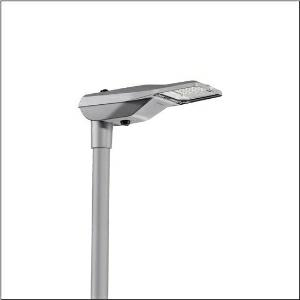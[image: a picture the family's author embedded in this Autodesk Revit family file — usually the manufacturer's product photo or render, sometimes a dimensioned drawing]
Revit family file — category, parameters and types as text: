
# Revit family: streetlight_sl_21_micro___p0_8a_5xe1u33t08db_8449
name_source: partatom
category: Lighting Fixtures
units: mm (PartAtom-declared; Revit-internal decimal feet)

## family parameters
Cut with Voids When Loaded = No
Host = Face
Light Source = No
Part Type = Normal
Room Calculation Point = No
Round Connector Dimension = Use Diameter
Shared = No

## types (1)
- --- (1 x LED, 5040 lm, 39.1 W, 3000K)
    Apparent Load = 39 VA
    CIE Flux Codes = 33 69 96 100 100
    Color Rendering = 70
    Color Temperature = 3000K
    Default Elevation = 1800 mm
    Description = Streetlight SL 21 micro, mast luminaire, primary light control with lens, of PMMA, primary optical cover: cover, of toughened safety glass, transparent, light distribution: P0.8a, light emission: direct distribution, primary light characteristic: asymmetric, installation type: post-top, side-entry, LED, High Power LED, rated luminous flux: 5.040lm, luminous efficacy: 129lm/W, light colour: 730, colour temperature: 3000K, control gear: D4i, control: pre-setting: logarithmic dimming characteristic, flexible luminous flux parameterisation, time-dependent luminous flux control, constant luminous flux control, overheat protection, mains connection: 220..240V, AC, 50/60Hz, start of lifetime: 39W, end of service life: 41W, reduction: 18W, luminaire housing, of diecast aluminium, powder-coated, Siteco® metallic grey (DB 702S), corrosivity category C5 mid according to DIN EN ISO 12944, multi-level sealing system, sealing non-destructively replaceable, inclination adjustable: 0°, 5°, 10°, 15°, please order mast flange separately, length: 528mm, width: 235mm, height: 110mm, mast flange for spigot size: 42mm (side-entry): 5XC10008XM4, 60/48mm (side-entry/post-top): 5XC10108XM2, 76/60mm (side-entry/post-top): 5XC10108XM1, Smart Interface below and above, protection rating (complete): IP66, insulation class (complete): insulation class II (safety insulation), certification: CE, ENEC, ENEC+, VDE, impact resistance: IK10, permissible operating ambient temperature for outdoor applications: -40..+50°C, standard-compliant lighting for roads and squares, packaging unit: 1 piece

Light Distribution: P0.8a
    Height = 110 mm
    Lamp = 1 x LED
    Lamp Light Flux = 5040 lm
    Lamp Power = 39.1 W
    Lamp count = 1
    Length = 528 mm
    Luminous efficacy = 129 lm/W
    Manufacturer = Siteco
    ModVariant = No
    Model = 5XE1U33T08DB
    Number of Poles = 1
    OnlyDefault = Yes
    Power Factor = 1
    Product Name = Streetlight SL 21 micro | P0.8a
    Product group = mast luminaire | pylon top
    ProductGroupID = 6100
    Protection Class = Protection class II
    Protection Degree = IP 66
    RLX_Detail_Level = 1
    RLX_Emergency_Light_Flux = 0 lm
    RLX_Emergency_Type = 0
    RLX_Emergency_Type_DB = No
    RlxData = <blob elided: 98617 chars, md5=6b190b65>
    Socket = socket
    Standby Power = 0 W
    System Light Flux = 5040 lm
    System Power = 39 W
    Type Comments = factory setting: luminous flux: 100 % | dim-lin: 254 | 765 mA
    Type Image = l_1007239.jpg
    URL = http://relux.com
    VarID = @adj_072776
    Voltage = 0 V
    Weight = 0.00 kg
    Width = 235 mm

## geometry (parser evidence)
native form markers: Blend x4, Sweep x10
no freeform markers — native parametric forms only
